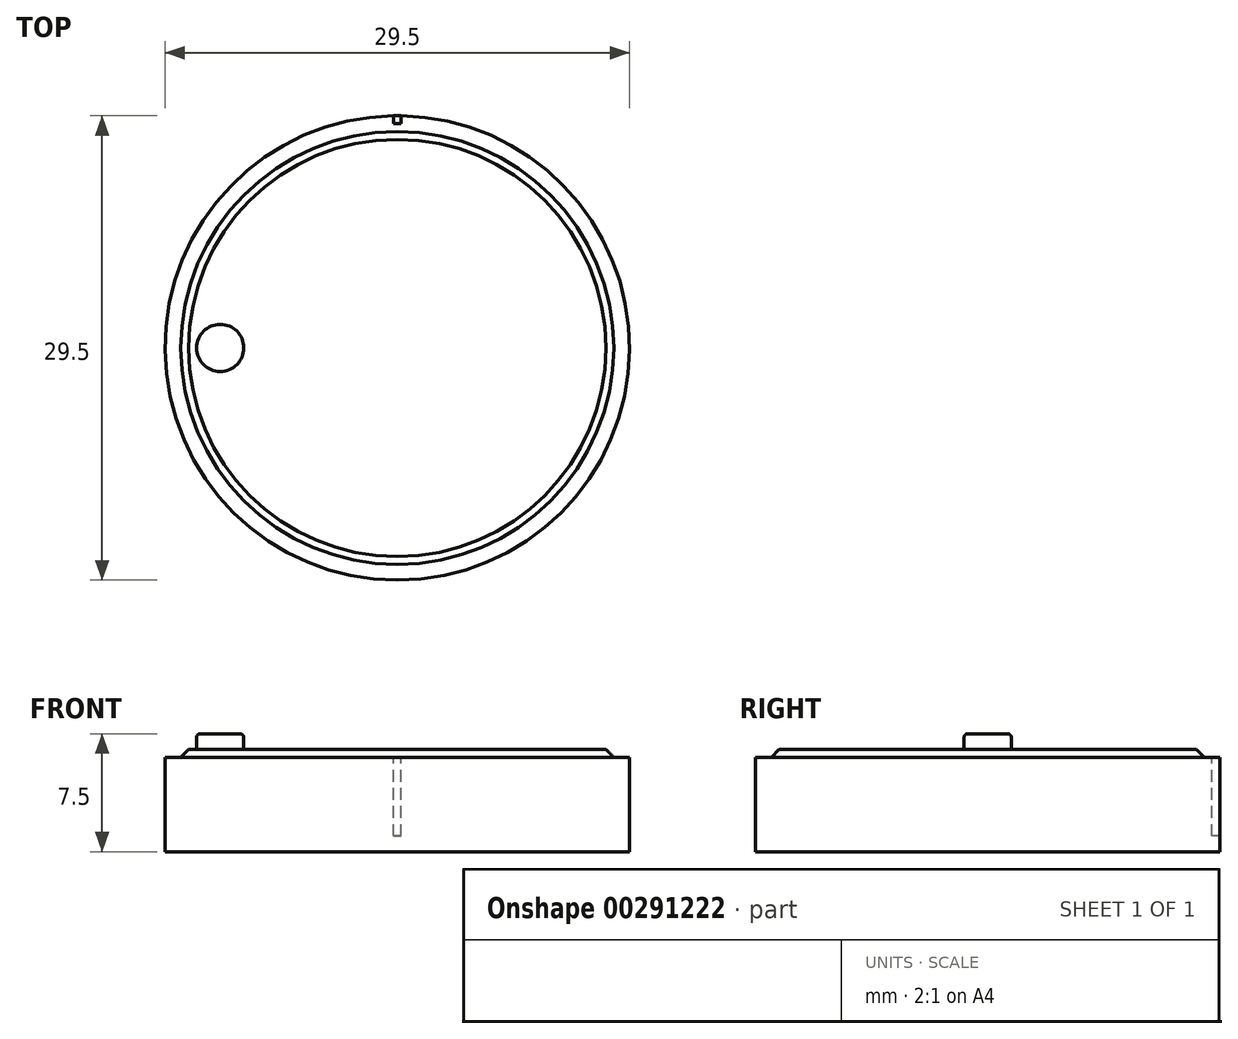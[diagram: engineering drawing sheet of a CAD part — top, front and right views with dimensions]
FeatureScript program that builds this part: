
annotation { "Feature Type Name" : "Feature", "Feature Type Description" : "" }
export const myFeature = defineFeature(function(context is Context, id is Id, definition is map)
    precondition{}
    {
        {
            var Q0;
            Q0=qCreatedBy(makeId("Top.planeOp"),FACE);
            var sketch = newSketch(context, id + "F0", { "sketchPlane" : qUnion([Q0])});
            skCircle(sketch, "E0", {"center": v(0, 0) * mm, "radius": 14.75 * mm});
            skSolve(sketch);
        }
        {
            var Q0;
            Q0 = qSketchRegion(id + "F0", true);
            extrude(context, id + "F1", {"entities" : qUnion([Q0]), "depth" : 6 * mm});
        }
        {
            var Q0;
            Q0=makeQuery(id+"F1.opExtrude","CAP_FACE",FACE,{"disambiguationData":[OSD([sQuery(id+"F0.wireOp",EDGE,"E0")])],"isStart":false});
            var sketch = newSketch(context, id + "F2", { "sketchPlane" : qUnion([Q0])});
            skLineSegment(sketch, "E1.bottom", {"start": v(-0.25, 15.25) * mm, "end": v(0.25, 15.25) * mm});
            skLineSegment(sketch, "E1.top", {"start": v(-0.25, 14.25) * mm, "end": v(0.25, 14.25) * mm});
            skLineSegment(sketch, "E1.left", {"start": v(-0.25, 15.25) * mm, "end": v(-0.25, 14.25) * mm});
            skLineSegment(sketch, "E1.right", {"start": v(0.25, 15.25) * mm, "end": v(0.25, 14.25) * mm});
            skPoint(sketch, "E1.middle", {"position": v(0, 14.75) * mm});
            skSolve(sketch);
        }
        {
            var Q0;
            {var subQ0=sQuery(id+"F2.wireOp",EDGE,"E1.top");Q0=makeQuery(id+"F2.imprint","IMPRINT",FACE,{"disambiguationData":[TD([[makeQuery(id+"F2.imprint","IMPRINT",EDGE,{"derivedFrom":subQ0}),1.0]])]});}
            extrude(context, id + "F3", {"entities" : qUnion([Q0]), "operationType" : NewBodyOperationType.REMOVE, "oppositeDirection" : true, "depth" : 5 * mm});
        }
        {
            var Q0;
            Q0=makeQuery(id+"F1.opExtrude","CAP_FACE",FACE,{"disambiguationData":[OSD([sQuery(id+"F0.wireOp",EDGE,"E0")])],"isStart":false});
            var sketch = newSketch(context, id + "F4", { "sketchPlane" : qUnion([Q0])});
            skCircle(sketch, "E2", {"center": v(0, 0) * mm, "radius": 13.75 * mm});
            skSolve(sketch);
        }
        {
            var Q0;
            Q0 = qSketchRegion(id + "F4", true);
            extrude(context, id + "F5", {"entities" : qUnion([Q0]), "operationType" : NewBodyOperationType.ADD, "depth" : 0.5 * mm});
        }
        {
            var Q0;
            Q0=makeQuery(id+"F5.opExtrude","CAP_FACE",FACE,{"disambiguationData":[OSD([sQuery(id+"F4.wireOp",EDGE,"E2")])],"isStart":false});
            var sketch = newSketch(context, id + "F6", { "sketchPlane" : qUnion([Q0])});
            skLineSegment(sketch, "E3", {"start": v(-13.75, 0) * mm, "end": v(-11.25, 0) * mm});
            skCircle(sketch, "E4", {"center": v(-11.25, 0) * mm, "radius": 1.5 * mm});
            skSolve(sketch);
        }
        {
            var Q0;
            Q0 = qSketchRegion(id + "F6", true);
            extrude(context, id + "F7", {"entities" : qUnion([Q0]), "operationType" : NewBodyOperationType.ADD, "depth" : 1 * mm});
        }
        {
            var Q0;
            Q0=makeQuery(id+"FI4fiMxGAmJ1jl2_1.7.F7.opExtrude","CAP_EDGE",EDGE,{"disambiguationData":[OSD([sQuery(id+"F6.wireOp",EDGE,"E4")])],"isStart":false});
            var Q1;
            Q1=makeQuery(id+"FI4fiMxGAmJ1jl2_1.6.F7.opExtrude","CAP_EDGE",EDGE,{"disambiguationData":[OSD([sQuery(id+"F6.wireOp",EDGE,"E4")])],"isStart":false});
            var Q2;
            Q2=makeQuery(id+"FI4fiMxGAmJ1jl2_1.5.F7.opExtrude","CAP_EDGE",EDGE,{"disambiguationData":[OSD([sQuery(id+"F6.wireOp",EDGE,"E4")])],"isStart":false});
            var Q3;
            Q3=makeQuery(id+"FI4fiMxGAmJ1jl2_1.4.F7.opExtrude","CAP_EDGE",EDGE,{"disambiguationData":[OSD([sQuery(id+"F6.wireOp",EDGE,"E4")])],"isStart":false});
            var Q4;
            Q4=makeQuery(id+"FI4fiMxGAmJ1jl2_1.3.F7.opExtrude","CAP_EDGE",EDGE,{"disambiguationData":[OSD([sQuery(id+"F6.wireOp",EDGE,"E4")])],"isStart":false});
            var Q5;
            Q5=makeQuery(id+"FI4fiMxGAmJ1jl2_1.2.F7.opExtrude","CAP_EDGE",EDGE,{"disambiguationData":[OSD([sQuery(id+"F6.wireOp",EDGE,"E4")])],"isStart":false});
            var Q6;
            Q6=makeQuery(id+"FI4fiMxGAmJ1jl2_1.1.F7.opExtrude","CAP_EDGE",EDGE,{"disambiguationData":[OSD([sQuery(id+"F6.wireOp",EDGE,"E4")])],"isStart":false});
            var Q7;
            Q7=makeQuery(id+"F7.opExtrude","CAP_EDGE",EDGE,{"disambiguationData":[OSD([sQuery(id+"F6.wireOp",EDGE,"E4")])],"isStart":false});
            var Q8;
            Q8=makeQuery(id+"FI4fiMxGAmJ1jl2_1.8.F7.opExtrude","CAP_EDGE",EDGE,{"disambiguationData":[OSD([sQuery(id+"F6.wireOp",EDGE,"E4")])],"isStart":false});
            fillet(context, id + "F8", {"entities" : qUnion([Q0, Q1, Q2, Q3, Q4, Q5, Q6, Q7, Q8]), "radius" : 0.25 * mm, "tangentPropagation" : true, "allowEdgeOverflow" : false});
        }
        {
            var Q0;
            Q0=makeQuery(id+"F5.opExtrude","CAP_EDGE",EDGE,{"disambiguationData":[OSD([sQuery(id+"F4.wireOp",EDGE,"E2")])],"isStart":false});
            chamfer(context, id + "F9", {"entities" : qUnion([Q0]), "width" : 0.5 * mm, "tangentPropagation" : true});
        }
    });
